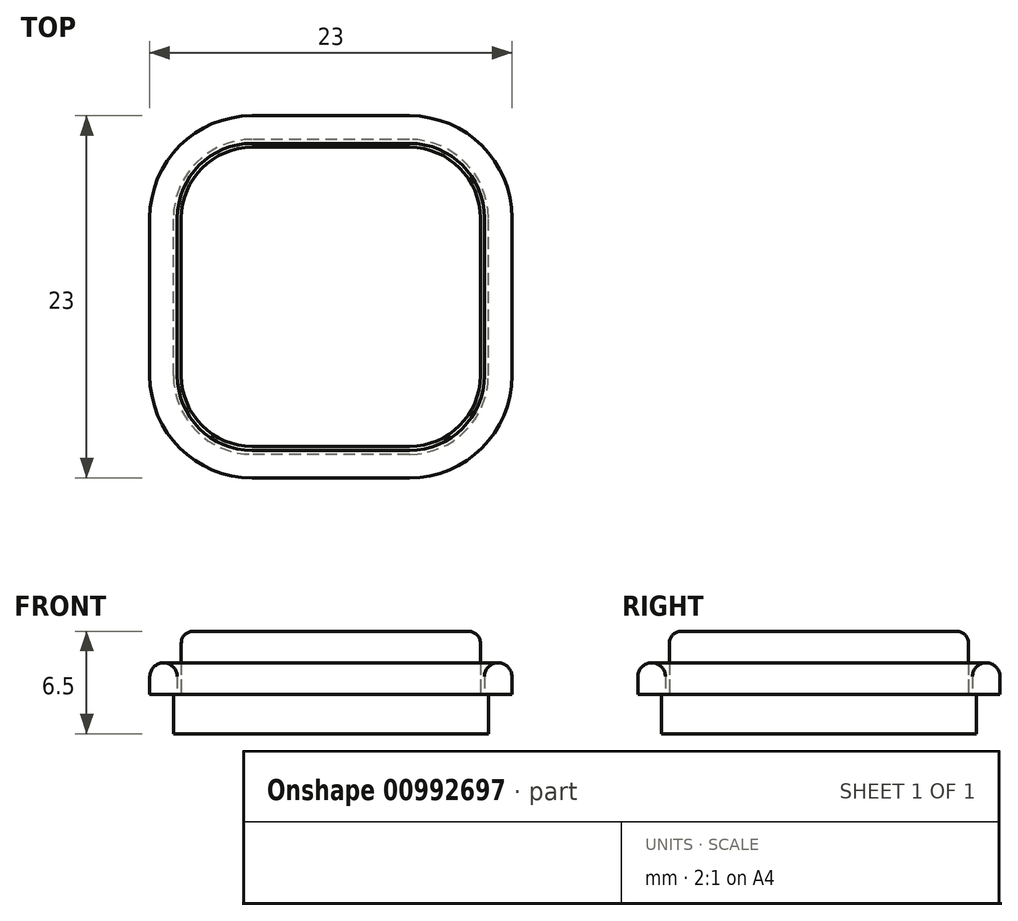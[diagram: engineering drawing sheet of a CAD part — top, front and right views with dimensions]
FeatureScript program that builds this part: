
annotation { "Feature Type Name" : "Feature", "Feature Type Description" : "" }
export const myFeature = defineFeature(function(context is Context, id is Id, definition is map)
    precondition{}
    {
        {
            var Q0;
            Q0=qCreatedBy(makeId("Top.planeOp"),FACE);
            var sketch = newSketch(context, id + "F0", { "sketchPlane" : qUnion([Q0])});
            skLineSegment(sketch, "E0.bottom", {"start": v(5, -10) * mm, "end": v(-5, -10) * mm});
            skLineSegment(sketch, "E0.top", {"start": v(5, 10) * mm, "end": v(-5, 10) * mm});
            skLineSegment(sketch, "E0.left", {"start": v(10, -5) * mm, "end": v(10, 5) * mm});
            skLineSegment(sketch, "E0.right", {"start": v(-10, -5) * mm, "end": v(-10, 5) * mm});
            skPoint(sketch, "E0.middle", {"position": v(0, 0) * mm});
            skPoint(sketch, "E1.visualSharp", {"position": v(-10, 10) * mm});
            skArc(sketch, "E1.filletArc", {"start": v(-5, 10) * mm, "mid": v(-8.54, 8.54) * mm, "end": v(-10, 5) * mm});
            skPoint(sketch, "E2.visualSharp", {"position": v(10, 10) * mm});
            skArc(sketch, "E2.filletArc", {"start": v(10, 5) * mm, "mid": v(8.54, 8.54) * mm, "end": v(5, 10) * mm});
            skPoint(sketch, "E3.visualSharp", {"position": v(10, -10) * mm});
            skArc(sketch, "E3.filletArc", {"start": v(5, -10) * mm, "mid": v(8.54, -8.54) * mm, "end": v(10, -5) * mm});
            skPoint(sketch, "E4.visualSharp", {"position": v(-10, -10) * mm});
            skArc(sketch, "E4.filletArc", {"start": v(-10, -5) * mm, "mid": v(-8.54, -8.54) * mm, "end": v(-5, -10) * mm});
            skSolve(sketch);
        }
        {
            var Q0;
            Q0=qSketchRegion(id+"F0",true);
            extrude(context, id + "F1", {"entities" : qUnion([Q0]), "depth" : 2.5 * mm, "offsetDistance" : 25 * mm});
        }
        {
            var Q0;
            Q0=makeQuery(id+"F1.opExtrude","CAP_FACE",FACE,{"disambiguationData":[OSD([sQuery(id+"F0.wireOp",EDGE,"E0.bottom"),sQuery(id+"F0.wireOp",EDGE,"E0.top"),sQuery(id+"F0.wireOp",EDGE,"E0.left"),sQuery(id+"F0.wireOp",EDGE,"E0.right"),sQuery(id+"F0.wireOp",EDGE,"E1.filletArc"),sQuery(id+"F0.wireOp",EDGE,"E2.filletArc"),sQuery(id+"F0.wireOp",EDGE,"E3.filletArc"),sQuery(id+"F0.wireOp",EDGE,"E4.filletArc")])],"isStart":false});
            var sketch = newSketch(context, id + "F2", { "sketchPlane" : qUnion([Q0])});
            skLineSegment(sketch, "E5.bottom", {"start": v(5, -11.5) * mm, "end": v(-5, -11.5) * mm});
            skLineSegment(sketch, "E5.top", {"start": v(5, 11.5) * mm, "end": v(-5, 11.5) * mm});
            skLineSegment(sketch, "E5.left", {"start": v(11.5, -5) * mm, "end": v(11.5, 5) * mm});
            skLineSegment(sketch, "E5.right", {"start": v(-11.5, -5) * mm, "end": v(-11.5, 5) * mm});
            skPoint(sketch, "E5.middle", {"position": v(0, 0) * mm});
            skPoint(sketch, "E6.visualSharp", {"position": v(-10, 10) * mm});
            skPoint(sketch, "E7.visualSharp", {"position": v(10, 10) * mm});
            skPoint(sketch, "E8.visualSharp", {"position": v(10, -10) * mm});
            skPoint(sketch, "E9.visualSharp", {"position": v(-10, -10) * mm});
            skPoint(sketch, "E10.visualSharp", {"position": v(-11.5, 11.5) * mm});
            skArc(sketch, "E10.filletArc", {"start": v(-5, 11.5) * mm, "mid": v(-9.6, 9.6) * mm, "end": v(-11.5, 5) * mm});
            skPoint(sketch, "E11.visualSharp", {"position": v(11.5, 11.5) * mm});
            skArc(sketch, "E11.filletArc", {"start": v(11.5, 5) * mm, "mid": v(9.6, 9.6) * mm, "end": v(5, 11.5) * mm});
            skPoint(sketch, "E12.visualSharp", {"position": v(11.5, -11.5) * mm});
            skArc(sketch, "E12.filletArc", {"start": v(5, -11.5) * mm, "mid": v(9.6, -9.6) * mm, "end": v(11.5, -5) * mm});
            skPoint(sketch, "E13.visualSharp", {"position": v(-11.5, -11.5) * mm});
            skArc(sketch, "E13.filletArc", {"start": v(-11.5, -5) * mm, "mid": v(-9.6, -9.6) * mm, "end": v(-5, -11.5) * mm});
            skLineSegment(sketch, "E14.bottom", {"start": v(5, -9.75) * mm, "end": v(-5, -9.75) * mm});
            skLineSegment(sketch, "E14.top", {"start": v(5, 9.75) * mm, "end": v(-5, 9.75) * mm});
            skLineSegment(sketch, "E14.left", {"start": v(9.75, -5) * mm, "end": v(9.75, 5) * mm});
            skLineSegment(sketch, "E14.right", {"start": v(-9.75, -5) * mm, "end": v(-9.75, 5) * mm});
            skPoint(sketch, "E15.visualSharp", {"position": v(-9.75, 9.75) * mm});
            skArc(sketch, "E15.filletArc", {"start": v(-5, 9.75) * mm, "mid": v(-8.36, 8.36) * mm, "end": v(-9.75, 5) * mm});
            skPoint(sketch, "E16.visualSharp", {"position": v(9.75, 9.75) * mm});
            skArc(sketch, "E16.filletArc", {"start": v(9.75, 5) * mm, "mid": v(8.36, 8.36) * mm, "end": v(5, 9.75) * mm});
            skPoint(sketch, "E17.visualSharp", {"position": v(9.75, -9.75) * mm});
            skArc(sketch, "E17.filletArc", {"start": v(5, -9.75) * mm, "mid": v(8.36, -8.36) * mm, "end": v(9.75, -5) * mm});
            skPoint(sketch, "E18.visualSharp", {"position": v(-9.75, -9.75) * mm});
            skArc(sketch, "E18.filletArc", {"start": v(-9.75, -5) * mm, "mid": v(-8.36, -8.36) * mm, "end": v(-5, -9.75) * mm});
            skSolve(sketch);
        }
        {
            var Q0;
            Q0=qSketchRegion(id+"F2",true);
            extrude(context, id + "F3", {"entities" : qUnion([Q0]), "operationType" : NewBodyOperationType.ADD, "depth" : 2 * mm, "offsetDistance" : 25 * mm});
        }
        {
            var Q0;
            Q0=makeQuery(id+"F3.opExtrude","CAP_EDGE",EDGE,{"disambiguationData":[OSD([sQuery(id+"F2.wireOp",EDGE,"E14.right")])],"isStart":false});
            var Q1;
            Q1=makeQuery(id+"F3.opExtrude","CAP_EDGE",EDGE,{"disambiguationData":[OSD([sQuery(id+"F2.wireOp",EDGE,"E5.right")])],"isStart":false});
            fillet(context, id + "F4", {"entities" : qUnion([Q0, Q1]), "radius" : .875 * mm, "tangentPropagation" : true, "allowEdgeOverflow" : false});
        }
        {
            var Q0;
            Q0=makeQuery(id+"F1.opExtrude","CAP_FACE",FACE,{"disambiguationData":[OSD([sQuery(id+"F0.wireOp",EDGE,"E0.bottom"),sQuery(id+"F0.wireOp",EDGE,"E0.top"),sQuery(id+"F0.wireOp",EDGE,"E0.left"),sQuery(id+"F0.wireOp",EDGE,"E0.right"),sQuery(id+"F0.wireOp",EDGE,"E1.filletArc"),sQuery(id+"F0.wireOp",EDGE,"E2.filletArc"),sQuery(id+"F0.wireOp",EDGE,"E3.filletArc"),sQuery(id+"F0.wireOp",EDGE,"E4.filletArc")])],"isStart":false});
            var sketch = newSketch(context, id + "F5", { "sketchPlane" : qUnion([Q0])});
            skLineSegment(sketch, "E19.bottom", {"start": v(5, 9.5) * mm, "end": v(-5, 9.5) * mm});
            skLineSegment(sketch, "E19.top", {"start": v(5, -9.5) * mm, "end": v(-5, -9.5) * mm});
            skLineSegment(sketch, "E19.left", {"start": v(9.5, 5) * mm, "end": v(9.5, -5) * mm});
            skLineSegment(sketch, "E19.right", {"start": v(-9.5, 5) * mm, "end": v(-9.5, -5) * mm});
            skPoint(sketch, "E19.middle", {"position": v(0, 0) * mm});
            skPoint(sketch, "E20.visualSharp", {"position": v(-9.5, 9.5) * mm});
            skArc(sketch, "E20.filletArc", {"start": v(-5, 9.5) * mm, "mid": v(-8.18, 8.18) * mm, "end": v(-9.5, 5) * mm});
            skPoint(sketch, "E21.visualSharp", {"position": v(9.5, 9.5) * mm});
            skArc(sketch, "E21.filletArc", {"start": v(9.5, 5) * mm, "mid": v(8.18, 8.18) * mm, "end": v(5, 9.5) * mm});
            skPoint(sketch, "E22.visualSharp", {"position": v(9.5, -9.5) * mm});
            skArc(sketch, "E22.filletArc", {"start": v(5, -9.5) * mm, "mid": v(8.18, -8.18) * mm, "end": v(9.5, -5) * mm});
            skPoint(sketch, "E23.visualSharp", {"position": v(-9.5, -9.5) * mm});
            skArc(sketch, "E23.filletArc", {"start": v(-9.5, -5) * mm, "mid": v(-8.18, -8.18) * mm, "end": v(-5, -9.5) * mm});
            skSolve(sketch);
        }
        {
            var Q0;
            Q0=qSketchRegion(id+"F5",true);
            extrude(context, id + "F6", {"entities" : qUnion([Q0]), "operationType" : NewBodyOperationType.ADD, "depth" : 4 * mm, "offsetDistance" : 25 * mm});
        }
        {
            var Q0;
            Q0=makeQuery(id+"F6.opExtrude","CAP_EDGE",EDGE,{"disambiguationData":[OSD([sQuery(id+"F5.wireOp",EDGE,"E19.top")])],"isStart":false});
            fillet(context, id + "F7", {"entities" : qUnion([Q0]), "radius" : .75 * mm, "tangentPropagation" : true, "allowEdgeOverflow" : false});
        }
    });
